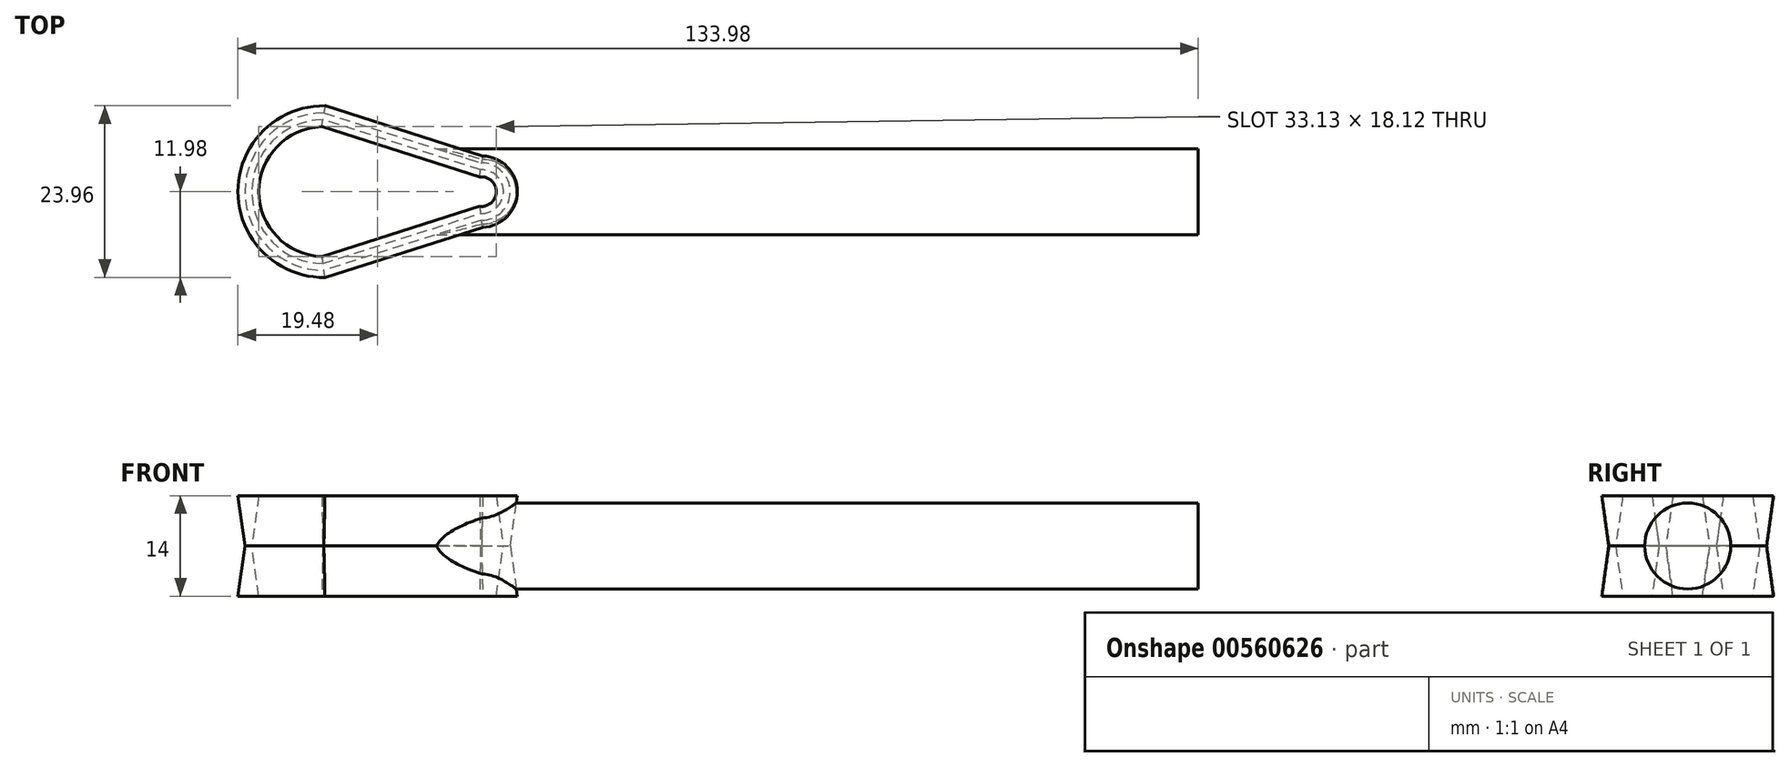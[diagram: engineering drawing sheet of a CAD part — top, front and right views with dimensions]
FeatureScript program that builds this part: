
annotation { "Feature Type Name" : "Feature", "Feature Type Description" : "" }
export const myFeature = defineFeature(function(context is Context, id is Id, definition is map)
    precondition{}
    {
        {
            var Q0;
            Q0=qCreatedBy(makeId("Top.planeOp"),FACE);
            var sketch = newSketch(context, id + "F0", { "sketchPlane" : qUnion([Q0])});
            skLineSegment(sketch, "E0", {"start": v(0, 0) * mm, "end": v(0, 6) * mm});
            skLineSegment(sketch, "E1", {"start": v(0, 6) * mm, "end": v(-100, 6) * mm});
            skLineSegment(sketch, "E2", {"start": v(-100, -6) * mm, "end": v(0, -6) * mm});
            skLineSegment(sketch, "E3", {"start": v(0, -6) * mm, "end": v(0, 6) * mm});
            skArc(sketch, "E4", {"start": v(-122, 11) * mm, "mid": v(-133, 0) * mm, "end": v(-122, -11) * mm});
            skPoint(sketch, "E4.centerSnap0", {"position": v(-100, 0) * mm});
            skArc(sketch, "E5", {"start": v(-100, -4) * mm, "mid": v(-96, 0) * mm, "end": v(-100, 4) * mm});
            skPoint(sketch, "E6.orphan", {"position": v(-122, 6) * mm});
            skLineSegment(sketch, "E7", {"start": v(-122, 11) * mm, "end": v(-100, 4) * mm});
            skLineSegment(sketch, "E8", {"start": v(-100, -4) * mm, "end": v(-122, -11) * mm});
            skArc(sketch, "E9.0", {"start": v(-100.14, -3.05) * mm, "mid": v(-96.95, 0) * mm, "end": v(-100.14, 3.05) * mm});
            skLineSegment(sketch, "E9.1", {"start": v(-100.14, -3.05) * mm, "end": v(-122.14, -10.05) * mm});
            skArc(sketch, "E9.2", {"start": v(-122.14, 10.05) * mm, "mid": v(-132.05, 0) * mm, "end": v(-122.14, -10.05) * mm});
            skLineSegment(sketch, "E9.3", {"start": v(-122.14, 10.05) * mm, "end": v(-100.14, 3.05) * mm});
            skSolve(sketch);
        }
        {
            var Q0;
            Q0 = qSketchRegion(id + "F0", true);
            extrude(context, id + "F1", {"entities" : qUnion([Q0]), "endBound" : BoundingType.SYMMETRIC, "depth" : 14 * mm, "offsetDistance" : 25 * mm, "hasDraft" : true, "draftAngle" : 8 * degree});
        }
        {
            var Q0;
            Q0=qCreatedBy(makeId("Right.planeOp"),FACE);
            var sketch = newSketch(context, id + "F2", { "sketchPlane" : qUnion([Q0])});
            skCircle(sketch, "E10", {"center": v(0, 0) * mm, "radius": 6 * mm});
            skSolve(sketch);
        }
        {
            var Q0;
            Q0 = qSketchRegion(id + "F2", true);
            extrude(context, id + "F3", {"entities" : qUnion([Q0]), "endBound" : BoundingType.UP_TO_NEXT, "oppositeDirection" : true, "depth" : 100 * mm, "offsetDistance" : 25 * mm});
        }
    });
